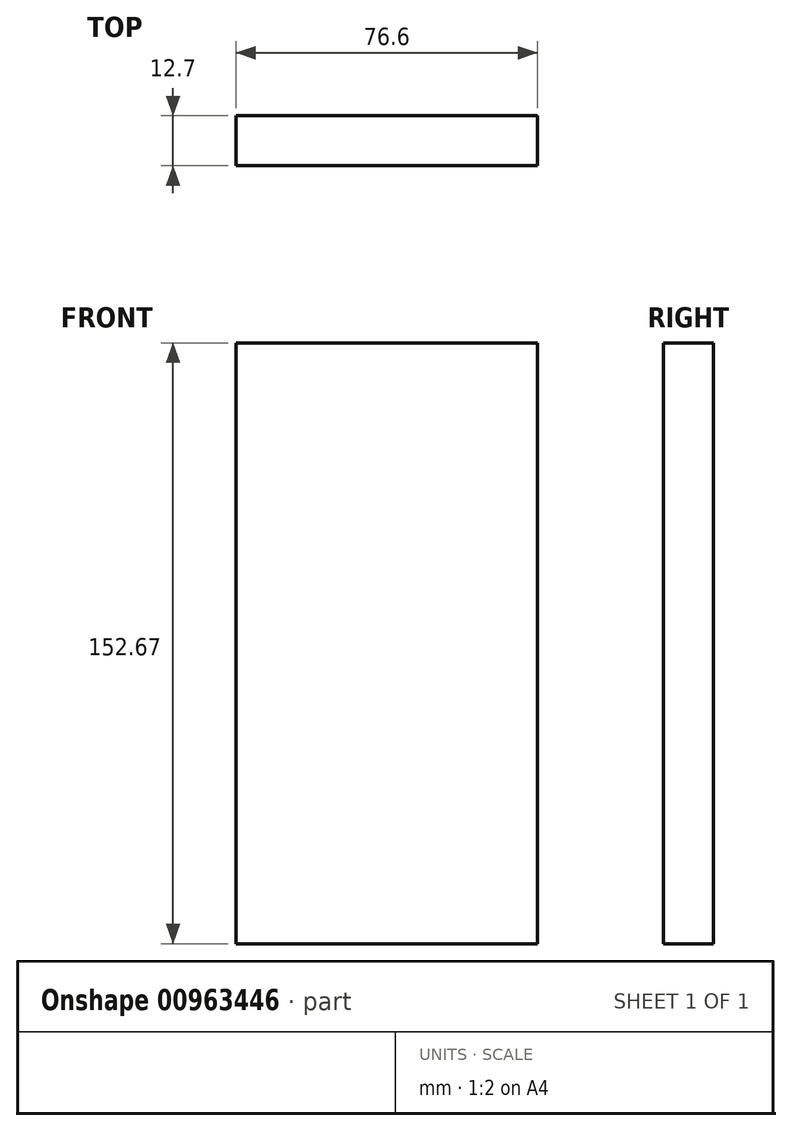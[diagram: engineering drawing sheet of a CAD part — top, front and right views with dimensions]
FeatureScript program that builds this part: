
annotation { "Feature Type Name" : "Feature", "Feature Type Description" : "" }
export const myFeature = defineFeature(function(context is Context, id is Id, definition is map)
    precondition{}
    {
        {
            var Q0;
            Q0=qCreatedBy(makeId("Front.planeOp"),FACE);
            var sketch = newSketch(context, id + "F0", { "sketchPlane" : qUnion([Q0])});
            skLineSegment(sketch, "E0", {"start": v(0, 0) * mm, "end": v(0, 76.45) * mm});
            skLineSegment(sketch, "E1", {"start": v(0, 76.45) * mm, "end": v(-38.3, 76.45) * mm});
            skLineSegment(sketch, "E2", {"start": v(-38.3, 76.45) * mm, "end": v(-38.3, -76.22) * mm});
            skLineSegment(sketch, "E3", {"start": v(-38.3, -76.22) * mm, "end": v(0, -76.22) * mm});
            skLineSegment(sketch, "E4", {"start": v(0, -76.22) * mm, "end": v(0, 0) * mm});
            skSolve(sketch);
        }
        {
            var Q0;
            Q0=makeQuery(id+"F0.imprint","IMPRINT",FACE,{"disambiguationData":[TD([[makeQuery(id+"F0.imprint","IMPRINT",EDGE,{"derivedFrom":sQuery(id+"F0.wireOp",EDGE,"E0")}),1.0]])]});
            extrude(context, id + "F1", {"entities" : qUnion([Q0]), "depth" : 12.7 * mm, "offsetDistance" : 25.4 * mm});
        }
        {
            var Q0;
            Q0=makeQuery(id+"F1.opExtrude","SWEPT_BODY",BODY,{"disambiguationData":[OSD([sQuery(id+"F0.wireOp",EDGE,"E0"),sQuery(id+"F0.wireOp",EDGE,"E1"),sQuery(id+"F0.wireOp",EDGE,"E2"),sQuery(id+"F0.wireOp",EDGE,"E3"),sQuery(id+"F0.wireOp",EDGE,"E4")])]});
            var Q1;
            Q1=qCreatedBy(makeId("Right.planeOp"),FACE);
            mirror(context, id + "F2", {"operationType" : NewBodyOperationType.ADD, "entities" : qUnion([Q0]), "mirrorPlane" : qUnion([Q1])});
        }
    });
